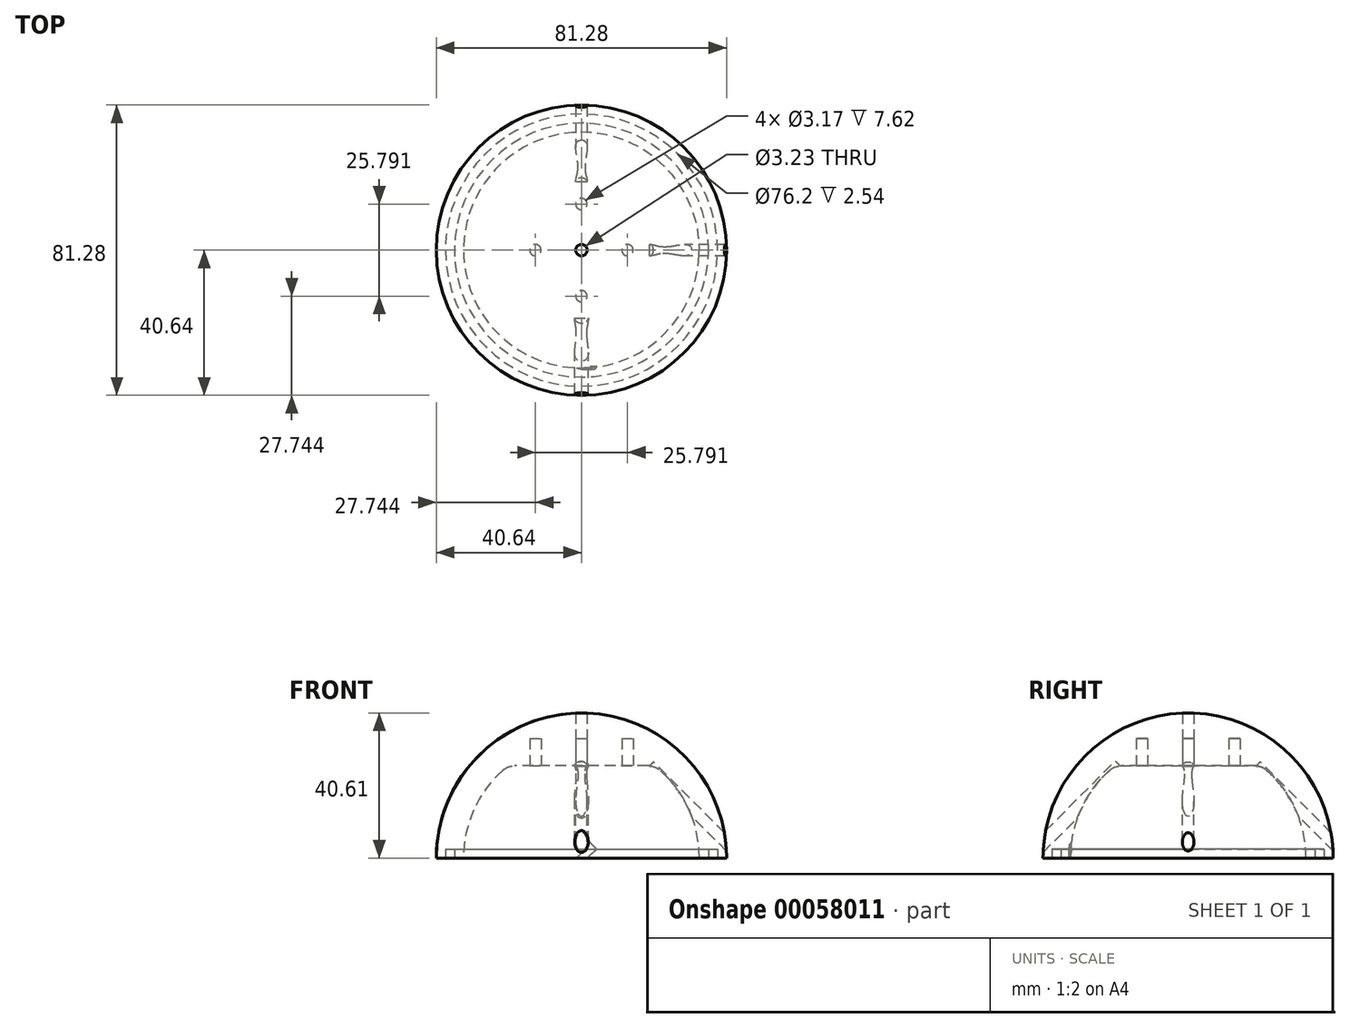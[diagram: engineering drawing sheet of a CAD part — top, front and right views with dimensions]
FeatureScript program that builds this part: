
annotation { "Feature Type Name" : "Feature", "Feature Type Description" : "" }
export const myFeature = defineFeature(function(context is Context, id is Id, definition is map)
    precondition{}
    {
        {
            var Q0;
            Q0=qCreatedBy(makeId("Front.planeOp"),FACE);
            var sketch = newSketch(context, id + "F0", { "sketchPlane" : qUnion([Q0])});
            skArc(sketch, "E0", {"start": v(40.64, 0) * mm, "mid": v(28.74, 28.74) * mm, "end": v(0, 40.64) * mm});
            skArc(sketch, "E1", {"start": v(33.02, 0) * mm, "mid": v(29.75, 14.33) * mm, "end": v(20.57, 25.83) * mm});
            skLineSegment(sketch, "E2", {"start": v(33.02, 0) * mm, "end": v(40.64, 0) * mm});
            skLineSegment(sketch, "E3", {"start": v(20.57, 25.83) * mm, "end": v(0, 25.83) * mm});
            skLineSegment(sketch, "E4", {"start": v(0, 25.83) * mm, "end": v(0, 40.64) * mm});
            skSolve(sketch);
        }
        {
            var Q0;
            Q0=makeQuery(id+"F0.imprint","IMPRINT",FACE,{"disambiguationData":[TD([[makeQuery(id+"F0.imprint","IMPRINT",EDGE,{"derivedFrom":sQuery(id+"F0.wireOp",EDGE,"E0")}),1.0]])]});
            var Q1;
            Q1=sQuery(id+"F0.wireOp",EDGE,"E4");
            revolve(context, id + "F1", {"entities" : qUnion([Q0]), "axis" : qUnion([Q1]), "revolveType" : RevolveType.FULL});
        }
        {
            var Q0;
            Q0=makeQuery(id+"F1.opRevolve","SWEPT_EDGE",EDGE,{"disambiguationData":[OSD([sQuery(id+"F0.wireOp",EDGE,"E1"),sQuery(id+"F0.wireOp",EDGE,"E3")])]});
            fillet(context, id + "F2", {"entities" : qUnion([Q0]), "radius" : 5.08 * mm, "tangentPropagation" : true, "allowEdgeOverflow" : false});
        }
        {
            var Q0;
            Q0=makeQuery(id+"F1.opRevolve","SWEPT_FACE",FACE,{"disambiguationData":[OSD([sQuery(id+"F0.wireOp",EDGE,"E3")])]});
            var sketch = newSketch(context, id + "F3", { "sketchPlane" : qUnion([Q0])});
            skCircle(sketch, "E5", {"center": v(0, 12.9) * mm, "radius": 1.59 * mm});
            skCircle(sketch, "E6.1.0", {"center": v(-12.9, 0) * mm, "radius": 1.59 * mm});
            skCircle(sketch, "E6.2.0", {"center": v(0, -12.9) * mm, "radius": 1.59 * mm});
            skCircle(sketch, "E6.3.0", {"center": v(12.9, 0) * mm, "radius": 1.59 * mm});
            skPoint(sketch, "E6.center", {"position": v(0, 0) * mm});
            skSolve(sketch);
        }
        {
            var Q0;
            Q0=makeQuery(id+"F1.opRevolve","SWEPT_FACE",FACE,{"disambiguationData":[OSD([sQuery(id+"F0.wireOp",EDGE,"E3")])]});
            var sketch = newSketch(context, id + "F4", { "sketchPlane" : qUnion([Q0])});
            skCircle(sketch, "E7", {"center": v(0, 0) * mm, "radius": 1.61 * mm});
            skSolve(sketch);
        }
        {
            var Q0;
            Q0 = qSketchRegion(id + "F4", true);
            extrude(context, id + "F5", {"entities" : qUnion([Q0]), "operationType" : NewBodyOperationType.REMOVE, "endBound" : BoundingType.THROUGH_ALL, "oppositeDirection" : true, "depth" : 25.4 * mm});
        }
        {
            var Q0;
            Q0 = qSketchRegion(id + "F3", true);
            extrude(context, id + "F6", {"entities" : qUnion([Q0]), "operationType" : NewBodyOperationType.REMOVE, "oppositeDirection" : true, "depth" : 7.62 * mm});
        }
        {
            var Q0;
            Q0=makeQuery(id+"F1.opRevolve","SWEPT_FACE",FACE,{"disambiguationData":[OSD([sQuery(id+"F0.wireOp",EDGE,"E2")])]});
            var sketch = newSketch(context, id + "F7", { "sketchPlane" : qUnion([Q0])});
            skCircle(sketch, "E8", {"center": v(0, 0) * mm, "radius": 38.1 * mm});
            skCircle(sketch, "E9", {"center": v(0, 0) * mm, "radius": 35.56 * mm});
            skSolve(sketch);
        }
        {
            var Q0;
            Q0 = qSketchRegion(id + "F7", true);
            extrude(context, id + "F8", {"entities" : qUnion([Q0]), "operationType" : NewBodyOperationType.REMOVE, "oppositeDirection" : true, "depth" : 2.54 * mm});
        }
        {
            var Q0;
            Q0=makeQuery(id+"F1.opRevolve","SWEPT_FACE",FACE,{"disambiguationData":[OSD([sQuery(id+"F0.wireOp",EDGE,"E3")])]});
            var sketch = newSketch(context, id + "F9", { "sketchPlane" : qUnion([Q0])});
            skLineSegment(sketch, "E10.rect.bottom", {"start": v(19.05, 19.05) * mm, "end": v(-19.05, 19.05) * mm});
            skLineSegment(sketch, "E10.rect.top", {"start": v(19.05, -19.05) * mm, "end": v(-19.05, -19.05) * mm});
            skLineSegment(sketch, "E10.rect.left", {"start": v(19.05, 19.05) * mm, "end": v(19.05, -19.05) * mm});
            skLineSegment(sketch, "E10.rect.right", {"start": v(-19.05, 19.05) * mm, "end": v(-19.05, -19.05) * mm});
            skPoint(sketch, "E10.rect.middle", {"position": v(0, 0) * mm});
            skSolve(sketch);
        }
        {
            var Q0;
            Q0=sQuery(id+"F9.wireOp",EDGE,"E10.rect.bottom");
            cPlane(context, id + "F10", {"entities" : qUnion([Q0]), "cplaneType" : CPlaneType.LINE_ANGLE, "offset" : 152.4 * mm, "angle" : 315 * degree, "width" : 152.4 * mm, "height" : 152.4 * mm});
        }
        {
            var Q0;
            Q0=qCreatedBy(id+"F10.planeOp",FACE);
            var sketch = newSketch(context, id + "F11", { "sketchPlane" : qUnion([Q0])});
            skPoint(sketch, "E11", {"position": v(0, 31.75) * mm});
            skSolve(sketch);
        }
        {
            var Q0;
            Q0=sQuery(id+"F11.wireOp",VERTEX,"E11");
            var Q1;
            Q1=makeQuery(id+"F1.opRevolve","SWEPT_BODY",BODY,{"disambiguationData":[OSD([sQuery(id+"F0.wireOp",EDGE,"E0"),sQuery(id+"F0.wireOp",EDGE,"E1"),sQuery(id+"F0.wireOp",EDGE,"E2"),sQuery(id+"F0.wireOp",EDGE,"E3"),sQuery(id+"F0.wireOp",EDGE,"E4")])]});
            hole(context, id + "F12", {"style" : HoleStyle.SIMPLE, "holeDiameter" : 3.8 * mm, "endStyle" : HoleEndStyle.THROUGH, "oppositeDirection" : true, "locations" : qUnion([Q0]), "scope" : qUnion([Q1])});
        }
        {
            var Q0;
            Q0=sQuery(id+"F9.wireOp",EDGE,"E10.rect.top");
            cPlane(context, id + "F13", {"entities" : qUnion([Q0]), "cplaneType" : CPlaneType.LINE_ANGLE, "offset" : 152.4 * mm, "angle" : 45 * degree, "width" : 152.4 * mm, "height" : 152.4 * mm});
        }
        {
            var Q0;
            Q0=qCreatedBy(id+"F13.planeOp",FACE);
            var sketch = newSketch(context, id + "F14", { "sketchPlane" : qUnion([Q0])});
            skPoint(sketch, "E12", {"position": v(0, 31.73) * mm});
            skSolve(sketch);
        }
        {
            var Q0;
            Q0=sQuery(id+"F14.wireOp",VERTEX,"E12");
            var Q1;
            Q1=makeQuery(id+"F1.opRevolve","SWEPT_BODY",BODY,{"disambiguationData":[OSD([sQuery(id+"F0.wireOp",EDGE,"E0"),sQuery(id+"F0.wireOp",EDGE,"E1"),sQuery(id+"F0.wireOp",EDGE,"E2"),sQuery(id+"F0.wireOp",EDGE,"E3"),sQuery(id+"F0.wireOp",EDGE,"E4")])]});
            hole(context, id + "F15", {"style" : HoleStyle.SIMPLE, "holeDiameter" : 3.23 * mm, "endStyle" : HoleEndStyle.THROUGH, "locations" : qUnion([Q0]), "scope" : qUnion([Q1])});
        }
        {
            var Q0;
            Q0=sQuery(id+"F9.wireOp",EDGE,"E10.rect.right");
            cPlane(context, id + "F16", {"entities" : qUnion([Q0]), "cplaneType" : CPlaneType.LINE_ANGLE, "offset" : 152.4 * mm, "angle" : 45 * degree, "width" : 152.4 * mm, "height" : 152.4 * mm});
        }
        {
            var Q0;
            Q0=qCreatedBy(id+"F16.planeOp",FACE);
            var sketch = newSketch(context, id + "F17", { "sketchPlane" : qUnion([Q0])});
            skPoint(sketch, "E13", {"position": v(-31.73, 0) * mm});
            skSolve(sketch);
        }
        {
            var Q0;
            Q0=sQuery(id+"F17.wireOp",VERTEX,"E13");
            var Q1;
            Q1=makeQuery(id+"F1.opRevolve","SWEPT_BODY",BODY,{"disambiguationData":[OSD([sQuery(id+"F0.wireOp",EDGE,"E0"),sQuery(id+"F0.wireOp",EDGE,"E1"),sQuery(id+"F0.wireOp",EDGE,"E2"),sQuery(id+"F0.wireOp",EDGE,"E3"),sQuery(id+"F0.wireOp",EDGE,"E4")])]});
            hole(context, id + "F18", {"style" : HoleStyle.SIMPLE, "holeDiameter" : 3.23 * mm, "endStyle" : HoleEndStyle.THROUGH, "locations" : qUnion([Q0]), "scope" : qUnion([Q1])});
        }
        {
            var Q0;
            Q0=sQuery(id+"F9.wireOp",EDGE,"E10.rect.left");
            cPlane(context, id + "F19", {"entities" : qUnion([Q0]), "cplaneType" : CPlaneType.LINE_ANGLE, "offset" : 152.4 * mm, "angle" : 315 * degree, "width" : 152.4 * mm, "height" : 152.4 * mm});
        }
        {
            var Q0;
            Q0=qCreatedBy(id+"F19.planeOp",FACE);
            var sketch = newSketch(context, id + "F20", { "sketchPlane" : qUnion([Q0])});
            skPoint(sketch, "E14", {"position": v(0, 31.72) * mm});
            skSolve(sketch);
        }
        {
            var Q0;
            Q0=sQuery(id+"F20.wireOp",VERTEX,"E14");
            var Q1;
            Q1=makeQuery(id+"F1.opRevolve","SWEPT_BODY",BODY,{"disambiguationData":[OSD([sQuery(id+"F0.wireOp",EDGE,"E0"),sQuery(id+"F0.wireOp",EDGE,"E1"),sQuery(id+"F0.wireOp",EDGE,"E2"),sQuery(id+"F0.wireOp",EDGE,"E3"),sQuery(id+"F0.wireOp",EDGE,"E4")])]});
            hole(context, id + "F21", {"style" : HoleStyle.SIMPLE, "holeDiameter" : 3.23 * mm, "endStyle" : HoleEndStyle.THROUGH, "locations" : qUnion([Q0]), "scope" : qUnion([Q1])});
        }
    });
